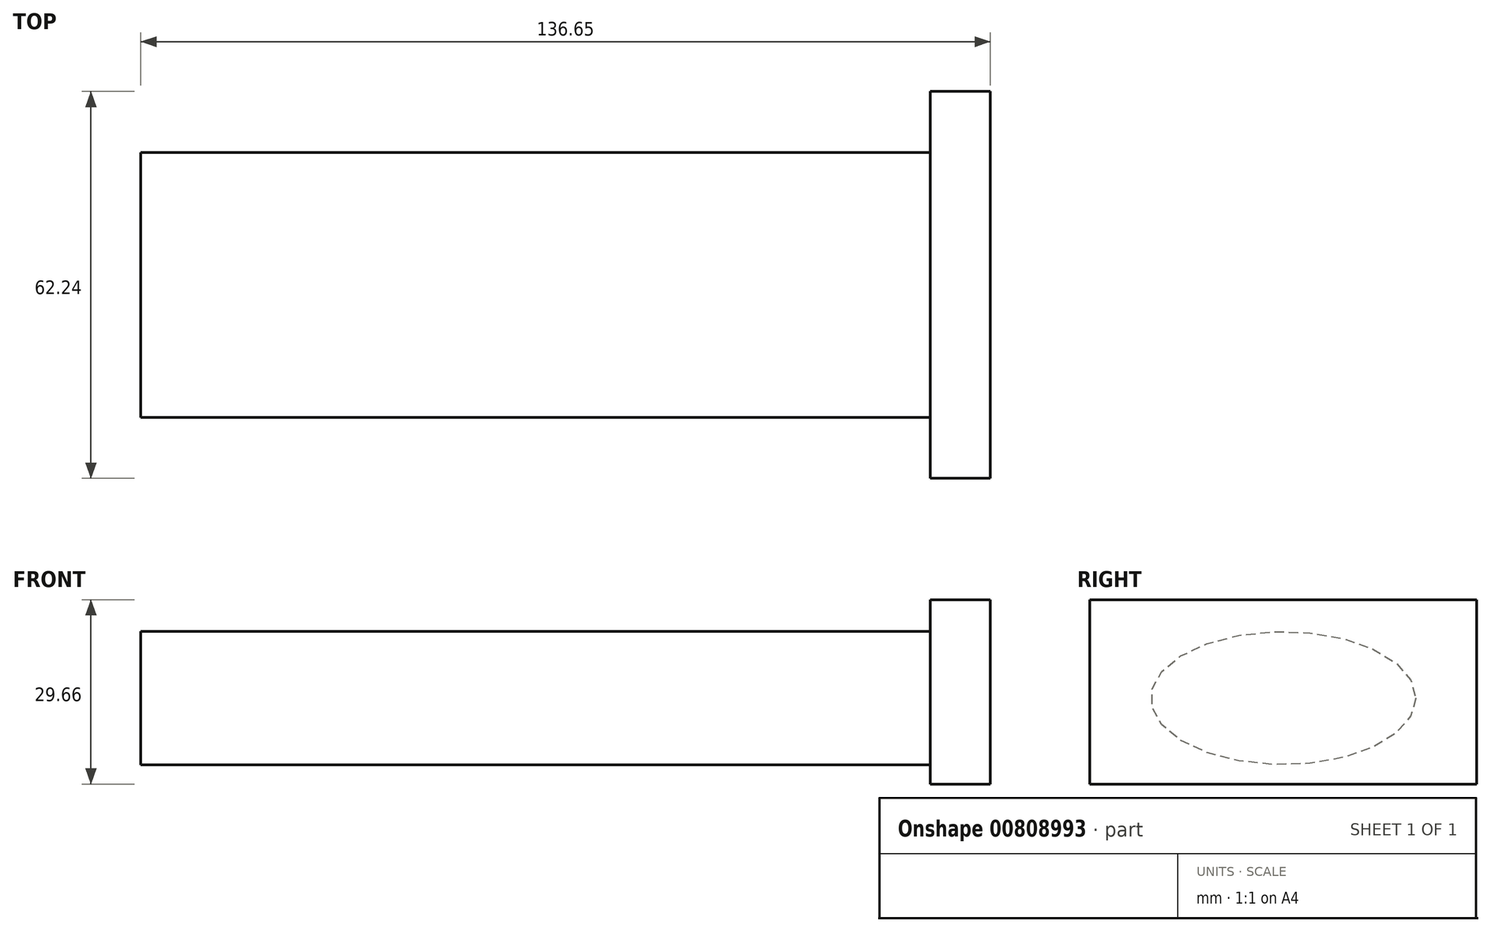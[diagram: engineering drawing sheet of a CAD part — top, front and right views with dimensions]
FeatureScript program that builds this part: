
annotation { "Feature Type Name" : "Feature", "Feature Type Description" : "" }
export const myFeature = defineFeature(function(context is Context, id is Id, definition is map)
    precondition{}
    {
        {
            var Q0;
            Q0=qCreatedBy(makeId("Right.planeOp"),FACE);
            var sketch = newSketch(context, id + "F0", { "sketchPlane" : qUnion([Q0])});
            skLineSegment(sketch, "E0.bottom", {"start": v(31.12, -44) * mm, "end": v(-31.12, -44) * mm});
            skLineSegment(sketch, "E0.top", {"start": v(31.12, -73.66) * mm, "end": v(-31.12, -73.66) * mm});
            skLineSegment(sketch, "E0.left", {"start": v(31.12, -44) * mm, "end": v(31.12, -73.66) * mm});
            skLineSegment(sketch, "E0.right", {"start": v(-31.12, -44) * mm, "end": v(-31.12, -73.66) * mm});
            skPoint(sketch, "E0.middle", {"position": v(0, -58.83) * mm});
            skSolve(sketch);
        }
        {
            var Q0;
            Q0=makeQuery(id+"F0.imprint","IMPRINT",FACE,{"disambiguationData":[TD([[makeQuery(id+"F0.imprint","IMPRINT",EDGE,{"derivedFrom":sQuery(id+"F0.wireOp",EDGE,"E0.bottom")}),1.0]])]});
            var sketch = newSketch(context, id + "F1", { "sketchPlane" : qUnion([Q0])});
            skSolve(sketch);
        }
        {
            var Q0;
            Q0=makeQuery(id+"F1.imprint","IMPRINT",FACE,{"disambiguationData":[TD([[makeQuery(id+"F1.imprint","IMPRINT",EDGE,{"derivedFrom":makeQuery(id+"F0.imprint","IMPRINT",EDGE,{"derivedFrom":sQuery(id+"F0.wireOp",EDGE,"E0.bottom")})}),1.0]])]});
            var Q1;
            Q1=makeQuery(id+"F0.imprint","IMPRINT",FACE,{"disambiguationData":[TD([[makeQuery(id+"F0.imprint","IMPRINT",EDGE,{"derivedFrom":sQuery(id+"F0.wireOp",EDGE,"E0.bottom")}),1.0]])]});
            extrude(context, id + "F2", {"entities" : qUnion([Q0, Q1]), "depth" : 9.65 * mm, "offsetDistance" : 25.4 * mm});
        }
        {
            var Q0;
            {var subQ0=sQuery(id+"F0.wireOp",EDGE,"E0.right");var subQ1=sQuery(id+"F0.wireOp",EDGE,"E0.left");var subQ2=sQuery(id+"F0.wireOp",EDGE,"E0.top");var subQ3=sQuery(id+"F0.wireOp",EDGE,"E0.bottom");Q0=makeQuery(id+"F2.opExtrude","CAP_FACE",FACE,{"disambiguationData":[OSD([subQ3,subQ2,subQ1,subQ0]),TDD([makeQuery(id+"F0.imprint","IMPRINT",EDGE,{"derivedFrom":subQ3}),makeQuery(id+"F0.imprint","IMPRINT",EDGE,{"derivedFrom":subQ2}),makeQuery(id+"F0.imprint","IMPRINT",EDGE,{"derivedFrom":subQ1}),makeQuery(id+"F0.imprint","IMPRINT",EDGE,{"derivedFrom":subQ0})])],"isStart":true});}
            var sketch = newSketch(context, id + "F3", { "sketchPlane" : qUnion([Q0])});
            skEllipse(sketch, "E1", {"center": v(0, -59.84) * mm, "majorRadius": 21.31 * mm, "minorRadius": 10.71 * mm, "majorAxis": v(-1, 0)});
            skSolve(sketch);
        }
        {
            var Q0;
            Q0=makeQuery(id+"F3.imprint","IMPRINT",FACE,{"disambiguationData":[TD([[makeQuery(id+"F3.imprint","IMPRINT",EDGE,{"derivedFrom":sQuery(id+"F3.wireOp",EDGE,"E1")}),1.0]])]});
            extrude(context, id + "F4", {"entities" : qUnion([Q0]), "depth" : 127 * mm, "offsetDistance" : 25.4 * mm});
        }
        {
            var Q0;
            {var subQ0=sQuery(id+"F0.wireOp",EDGE,"E0.right");var subQ1=sQuery(id+"F0.wireOp",EDGE,"E0.left");var subQ2=sQuery(id+"F0.wireOp",EDGE,"E0.top");var subQ3=sQuery(id+"F0.wireOp",EDGE,"E0.bottom");Q0=makeQuery(id+"F2.opExtrude","CAP_FACE",FACE,{"disambiguationData":[OSD([subQ3,subQ2,subQ1,subQ0]),TDD([makeQuery(id+"F0.imprint","IMPRINT",EDGE,{"derivedFrom":subQ3}),makeQuery(id+"F0.imprint","IMPRINT",EDGE,{"derivedFrom":subQ2}),makeQuery(id+"F0.imprint","IMPRINT",EDGE,{"derivedFrom":subQ1}),makeQuery(id+"F0.imprint","IMPRINT",EDGE,{"derivedFrom":subQ0})])],"isStart":true});}
            var sketch = newSketch(context, id + "F5", { "sketchPlane" : qUnion([Q0])});
            skCircle(sketch, "E2", {"center": v(-27.01, -61.2) * mm, "radius": 2.55 * mm});
            skSolve(sketch);
        }
        {
            var Q0;
            Q0=sQuery(id+"F5.wireOp",EDGE,"E2");
            extrude(context, id + "F6", {"bodyType" : ToolBodyType.SURFACE, "surfaceEntities" : qUnion([Q0]), "depth" : -25.4 * mm, "offsetDistance" : 25.4 * mm});
        }
    });
